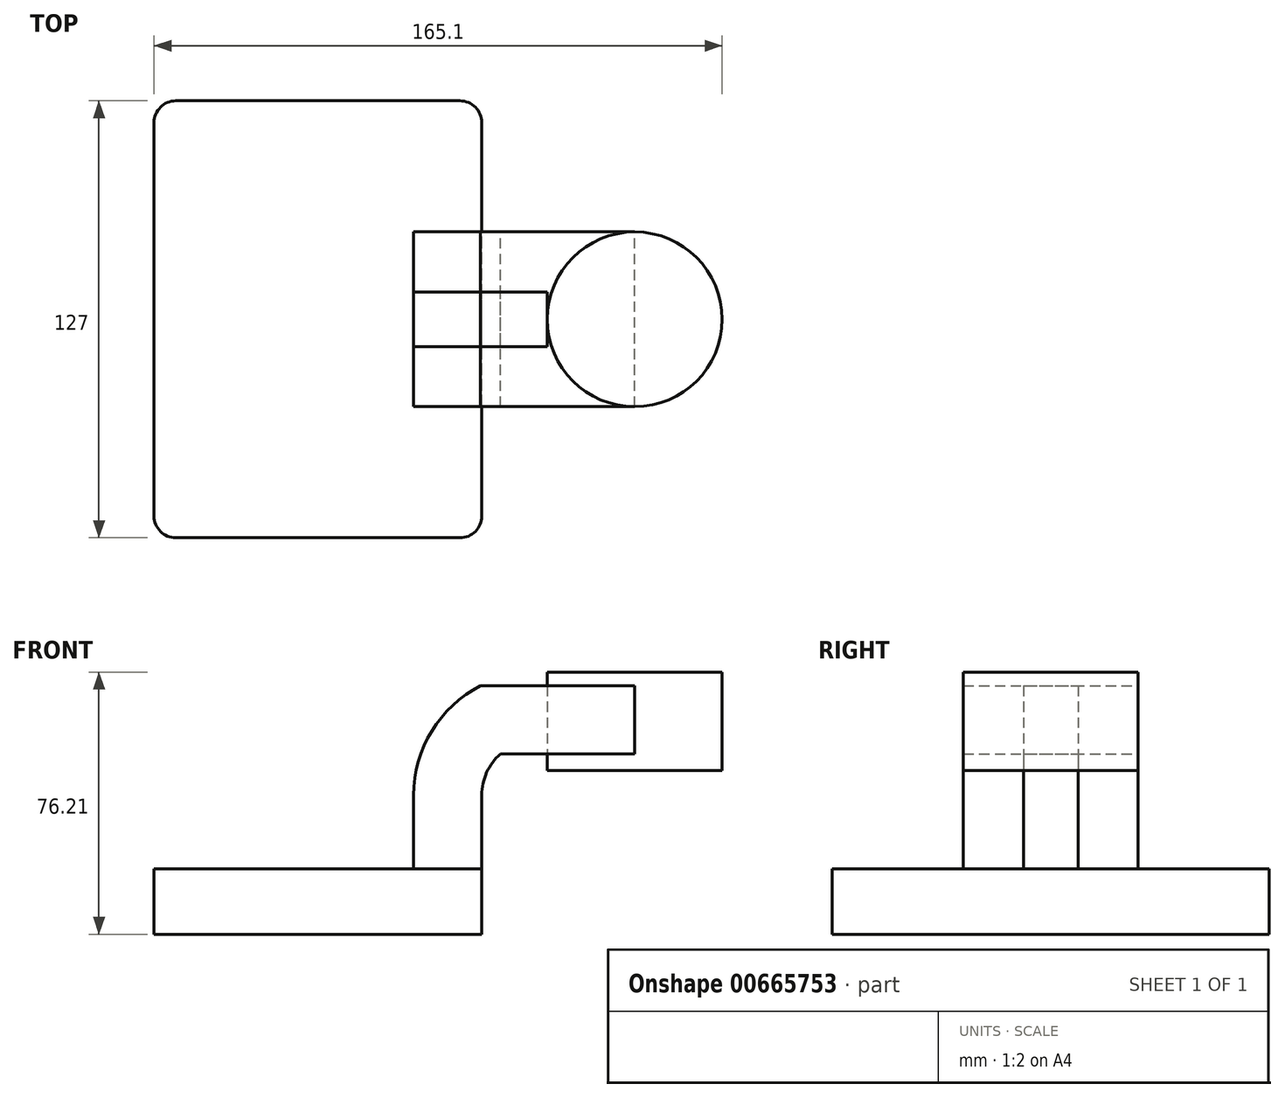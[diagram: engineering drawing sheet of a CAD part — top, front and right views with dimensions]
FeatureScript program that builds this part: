
annotation { "Feature Type Name" : "Feature", "Feature Type Description" : "" }
export const myFeature = defineFeature(function(context is Context, id is Id, definition is map)
    precondition{}
    {
        {
            var Q0;
            Q0=qCreatedBy(makeId("Front.planeOp"),FACE);
            var sketch = newSketch(context, id + "F0", { "sketchPlane" : qUnion([Q0])});
            skLineSegment(sketch, "E0.bottom", {"start": v(-47.62, -9.53) * mm, "end": v(47.63, -9.53) * mm});
            skLineSegment(sketch, "E0.top", {"start": v(-47.62, 9.52) * mm, "end": v(47.63, 9.52) * mm});
            skLineSegment(sketch, "E0.left", {"start": v(-47.62, -9.53) * mm, "end": v(-47.62, 9.52) * mm});
            skLineSegment(sketch, "E0.right", {"start": v(47.63, -9.53) * mm, "end": v(47.63, 9.52) * mm});
            skPoint(sketch, "E0.middle", {"position": v(0, 0) * mm});
            skLineSegment(sketch, "E1.bottom", {"start": v(66.68, 66.67) * mm, "end": v(117.48, 66.67) * mm});
            skLineSegment(sketch, "E1.top", {"start": v(66.68, 38.1) * mm, "end": v(117.48, 38.1) * mm});
            skLineSegment(sketch, "E1.left", {"start": v(66.68, 66.67) * mm, "end": v(66.68, 38.1) * mm});
            skLineSegment(sketch, "E1.right", {"start": v(117.48, 66.67) * mm, "end": v(117.48, 38.1) * mm});
            skPoint(sketch, "E1.middle", {"position": v(92.08, 52.39) * mm});
            skLineSegment(sketch, "E2", {"start": v(47.63, 9.52) * mm, "end": v(47.63, 30.9) * mm});
            skArc(sketch, "E3", {"start": v(47.63, 30.9) * mm, "mid": v(49.05, 37.48) * mm, "end": v(53.07, 42.88) * mm});
            skLineSegment(sketch, "E4", {"start": v(53.07, 42.88) * mm, "end": v(92.08, 42.88) * mm});
            skLineSegment(sketch, "E5.0", {"start": v(47.27, 62.66) * mm, "end": v(92.08, 62.66) * mm});
            skArc(sketch, "E5.1", {"start": v(27.84, 30.9) * mm, "mid": v(33.08, 49.52) * mm, "end": v(47.27, 62.66) * mm});
            skLineSegment(sketch, "E5.2", {"start": v(27.84, 9.52) * mm, "end": v(27.84, 30.9) * mm});
            skFitSpline(sketch, "E6", {"points": [v(-47.62, 9.52) * mm, v(47.27, 62.66) * mm], "startDerivative": vector(2.4, 106.32) * mm, "endDerivative": vector(141.8, 1.37) * mm});
            skLineSegment(sketch, "E7", {"start": v(92.08, 38.1) * mm, "end": v(92.08, 66.67) * mm});
            skSolve(sketch);
        }
        {
            var Q0;
            Q0=makeQuery(id+"F0.imprint","IMPRINT",FACE,{"disambiguationData":[TD([[makeQuery(id+"F0.imprint","IMPRINT",EDGE,{"derivedFrom":sQuery(id+"F0.wireOp",EDGE,"E0.bottom")}),1.0]])]});
            extrude(context, id + "F1", {"entities" : qUnion([Q0]), "depth" : 127 * mm, "offsetDistance" : 25.4 * mm, "symmetric" : true});
        }
        {
            var Q0;
            {var subQ0=sQuery(id+"F0.wireOp",EDGE,"E2");Q0=makeQuery(id+"F0.imprint","IMPRINT",FACE,{"disambiguationData":[TD([[makeQuery(id+"F0.imprint","IMPRINT",EDGE,{"derivedFrom":subQ0}),1.0]])]});}
            var Q1;
            {var subQ5=sQuery(id+"F0.wireOp",EDGE,"j164lFBo-gCPK-DbU2-IHz8-SBUVrSm6E4J3");Q1=makeQuery(id+"F0.imprint","IMPRINT",FACE,{"disambiguationData":[TD([[makeQuery(id+"F0.imprint","IMPRINT",EDGE,{"derivedFrom":subQ5}),1.0]])]});}
            var Q2;
            {var subQ0=sQuery(id+"F0.wireOp",EDGE,"E5.0");var subQ1=sQuery(id+"F0.wireOp",EDGE,"E1.left");var subQ2=makeQuery(id+"F0.imprint","INTERSECT",VERTEX,{"derivedFrom":[subQ1,subQ0]});Q2=makeQuery(id+"F0.imprint","IMPRINT",FACE,{"disambiguationData":[TD([[makeQuery(id+"F0.imprint","IMPRINT",EDGE,{"disambiguationData":[TD([[subQ2,-1.0]])],"derivedFrom":subQ1}),1.0]])]});}
            extrude(context, id + "F2", {"entities" : qUnion([Q0, Q1, Q2]), "depth" : 50.8 * mm, "offsetDistance" : 25.4 * mm, "symmetric" : true});
        }
        {
            var Q0;
            Q0=makeQuery(id+"F0.imprint","IMPRINT",FACE,{"disambiguationData":[TD([[makeQuery(id+"F0.imprint","IMPRINT",EDGE,{"derivedFrom":sQuery(id+"F0.wireOp",EDGE,"E5.1")}),1.0]])]});
            extrude(context, id + "F3", {"entities" : qUnion([Q0]), "depth" : 15.88 * mm, "offsetDistance" : 25.4 * mm, "symmetric" : true});
        }
        {
            var Q0;
            {var subQ4=sQuery(id+"F0.wireOp",EDGE,"E1.right");Q0=makeQuery(id+"F0.imprint","IMPRINT",FACE,{"disambiguationData":[TD([[makeQuery(id+"F0.imprint","IMPRINT",EDGE,{"derivedFrom":subQ4}),-1.0]])]});}
            var Q1;
            Q1=sQuery(id+"F0.wireOp",EDGE,"E7");
            revolve(context, id + "F4", {"entities" : qUnion([Q0]), "axis" : qUnion([Q1]), "revolveType" : RevolveType.FULL});
        }
        {
            var Q0;
            Q0=makeQuery(id+"F1.opExtrude","CAP_EDGE",EDGE,{"disambiguationData":[OSD([sQuery(id+"F0.wireOp",EDGE,"E0.right")])],"isStart":false});
            var Q1;
            Q1=makeQuery(id+"F1.opExtrude","CAP_EDGE",EDGE,{"disambiguationData":[OSD([sQuery(id+"F0.wireOp",EDGE,"E0.left")])],"isStart":false});
            var Q2;
            Q2=makeQuery(id+"F1.opExtrude","CAP_EDGE",EDGE,{"disambiguationData":[OSD([sQuery(id+"F0.wireOp",EDGE,"E0.left")])],"isStart":true});
            var Q3;
            Q3=makeQuery(id+"F1.opExtrude","CAP_EDGE",EDGE,{"disambiguationData":[OSD([sQuery(id+"F0.wireOp",EDGE,"E0.right")])],"isStart":true});
            fillet(context, id + "F5", {"entities" : qUnion([Q0, Q1, Q2, Q3]), "radius" : 6.35 * mm, "tangentPropagation" : true, "allowEdgeOverflow" : false});
        }
    });
